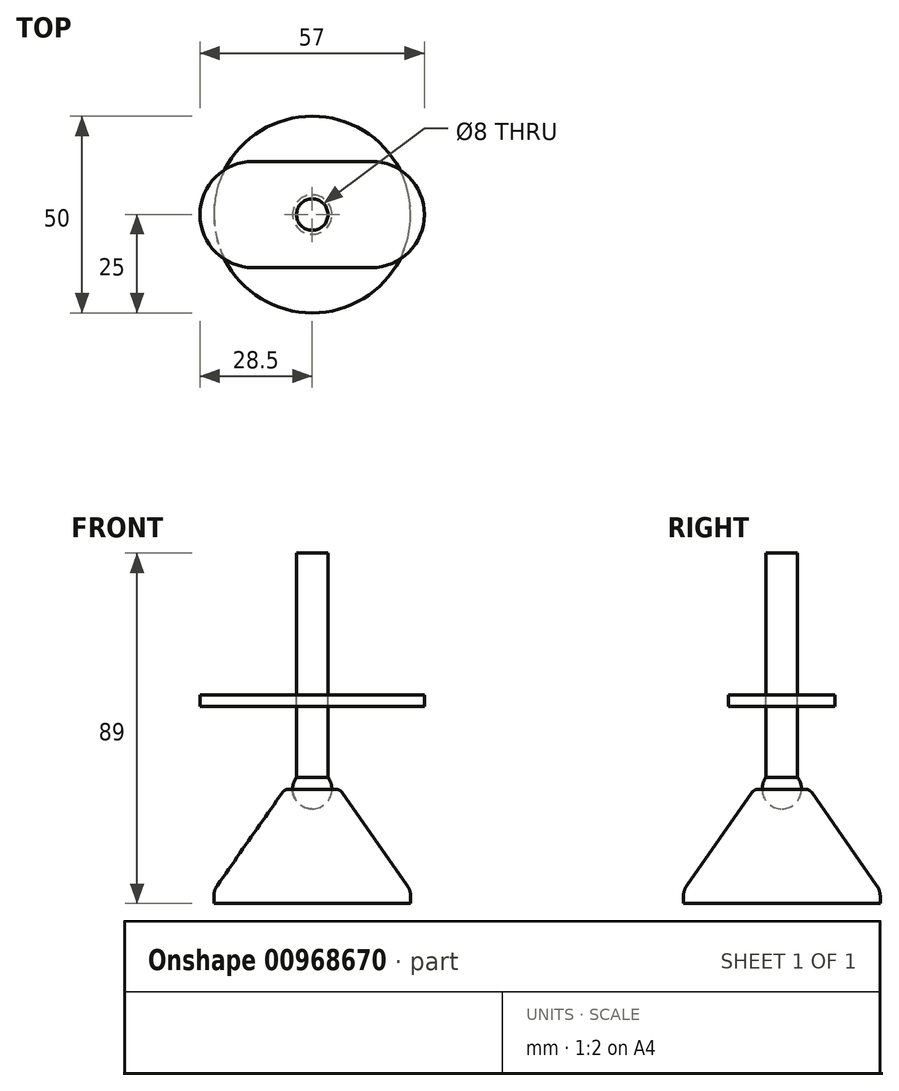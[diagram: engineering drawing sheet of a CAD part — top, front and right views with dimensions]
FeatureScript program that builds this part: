
annotation { "Feature Type Name" : "Feature", "Feature Type Description" : "" }
export const myFeature = defineFeature(function(context is Context, id is Id, definition is map)
    precondition{}
    {
        {
            var Q0;
            Q0=qCreatedBy(makeId("Front.planeOp"),FACE);
            var sketch = newSketch(context, id + "F0", { "sketchPlane" : qUnion([Q0])});
            skLineSegment(sketch, "E0", {"start": v(0, 0) * mm, "end": v(-25, 0) * mm});
            skLineSegment(sketch, "E1", {"start": v(0, 0) * mm, "end": v(0, 29) * mm, "construction": true});
            skArc(sketch, "E2", {"start": v(-5, 29) * mm, "mid": v(-3.54, 25.46) * mm, "end": v(0, 24) * mm});
            skLineSegment(sketch, "E3", {"start": v(0, 24) * mm, "end": v(0, 0) * mm});
            skLineSegment(sketch, "E4", {"start": v(-25, 0) * mm, "end": v(-25, 1.7) * mm});
            skLineSegment(sketch, "E5", {"start": v(-5, 29) * mm, "end": v(-5.96, 29) * mm});
            skLineSegment(sketch, "E6", {"start": v(-7.6, 28.15) * mm, "end": v(-24.1, 4.57) * mm});
            skPoint(sketch, "E7.visualSharp", {"position": v(-7, 29) * mm});
            skArc(sketch, "E7.filletArc", {"start": v(-5.96, 29) * mm, "mid": v(-6.88, 28.77) * mm, "end": v(-7.6, 28.15) * mm});
            skPoint(sketch, "E8.visualSharp", {"position": v(-25, 3.28) * mm});
            skArc(sketch, "E8.filletArc", {"start": v(-24.1, 4.57) * mm, "mid": v(-24.77, 3.2) * mm, "end": v(-25, 1.7) * mm});
            skSolve(sketch);
        }
        {
            var Q0;
            Q0=makeQuery(id+"F0.imprint","IMPRINT",FACE,{"disambiguationData":[TD([[makeQuery(id+"F0.imprint","IMPRINT",EDGE,{"derivedFrom":sQuery(id+"F0.wireOp",EDGE,"E0")}),-1.0]])]});
            var Q1;
            Q1=sQuery(id+"F0.wireOp",EDGE,"E1");
            revolve(context, id + "F1", {"surfaceOperationType" : NewSurfaceOperationType.NEW, "entities" : qUnion([Q0]), "axis" : qUnion([Q1]), "revolveType" : RevolveType.FULL});
        }
        {
            var Q0;
            Q0=qCreatedBy(makeId("Front.planeOp"),FACE);
            var sketch = newSketch(context, id + "F2", { "sketchPlane" : qUnion([Q0])});
            skArc(sketch, "E9.0", {"start": v(-5, 29) * mm, "mid": v(-3.54, 25.46) * mm, "end": v(0, 24) * mm, "construction": true});
            skArc(sketch, "E10", {"start": v(-4, 32) * mm, "mid": v(-4.47, 26.76) * mm, "end": v(0, 24) * mm});
            skLineSegment(sketch, "E11.top", {"start": v(0, 89) * mm, "end": v(-4, 89) * mm});
            skLineSegment(sketch, "E11.left", {"start": v(0, 34) * mm, "end": v(0, 89) * mm});
            skLineSegment(sketch, "E11.right", {"start": v(-4, 32) * mm, "end": v(-4, 89) * mm});
            skLineSegment(sketch, "E12", {"start": v(0, 34) * mm, "end": v(0, 24) * mm});
            skSolve(sketch);
        }
        {
            var Q0;
            Q0=makeQuery(id+"F2.imprint","IMPRINT",FACE,{"disambiguationData":[TD([[makeQuery(id+"F2.imprint","IMPRINT",EDGE,{"derivedFrom":sQuery(id+"F2.wireOp",EDGE,"E10")}),1.0]])]});
            var Q1;
            Q1=sQuery(id+"F2.wireOp",EDGE,"E12");
            revolve(context, id + "F3", {"surfaceOperationType" : NewSurfaceOperationType.NEW, "entities" : qUnion([Q0]), "axis" : qUnion([Q1]), "revolveType" : RevolveType.FULL});
        }
        {
            var Q0;
            Q0=qCreatedBy(makeId("Top.planeOp"),FACE);
            cPlane(context, id + "F4", {"entities" : qUnion([Q0]), "cplaneType" : CPlaneType.OFFSET, "offset" : 50 * mm, "width" : 150 * mm, "height" : 150 * mm});
        }
        {
            var Q0;
            Q0=qCreatedBy(id+"F4.planeOp",FACE);
            var sketch = newSketch(context, id + "F5", { "sketchPlane" : qUnion([Q0])});
            skLineSegment(sketch, "E13.bottom", {"start": v(-15, 13.5) * mm, "end": v(15, 13.5) * mm});
            skLineSegment(sketch, "E13.top", {"start": v(-15, -13.5) * mm, "end": v(15, -13.5) * mm});
            skLineSegment(sketch, "E13.left", {"start": v(-28.5, 0) * mm, "end": v(-28.5, 0) * mm});
            skLineSegment(sketch, "E13.right", {"start": v(28.5, 0) * mm, "end": v(28.5, 0) * mm});
            skPoint(sketch, "E13.middle", {"position": v(0, 0) * mm});
            skPoint(sketch, "E14.visualSharp", {"position": v(-28.5, 13.5) * mm});
            skArc(sketch, "E14.filletArc", {"start": v(-15, 13.5) * mm, "mid": v(-24.55, 9.55) * mm, "end": v(-28.5, 0) * mm});
            skPoint(sketch, "E15.visualSharp", {"position": v(-28.5, -13.5) * mm});
            skArc(sketch, "E15.filletArc", {"start": v(-28.5, 0) * mm, "mid": v(-24.55, -9.55) * mm, "end": v(-15, -13.5) * mm});
            skPoint(sketch, "E16.visualSharp", {"position": v(28.5, -13.5) * mm});
            skArc(sketch, "E16.filletArc", {"start": v(15, -13.5) * mm, "mid": v(24.55, -9.55) * mm, "end": v(28.5, 0) * mm});
            skPoint(sketch, "E17.visualSharp", {"position": v(28.5, 13.5) * mm});
            skArc(sketch, "E17.filletArc", {"start": v(28.5, 0) * mm, "mid": v(24.55, 9.55) * mm, "end": v(15, 13.5) * mm});
            skCircle(sketch, "E18", {"center": v(0, 0) * mm, "radius": 4 * mm});
            skSolve(sketch);
        }
        {
            var Q0;
            Q0=qSketchRegion(id+"F5",true);
            extrude(context, id + "F6", {"entities" : qUnion([Q0]), "depth" : 3 * mm, "offsetDistance" : 25 * mm});
        }
    });
